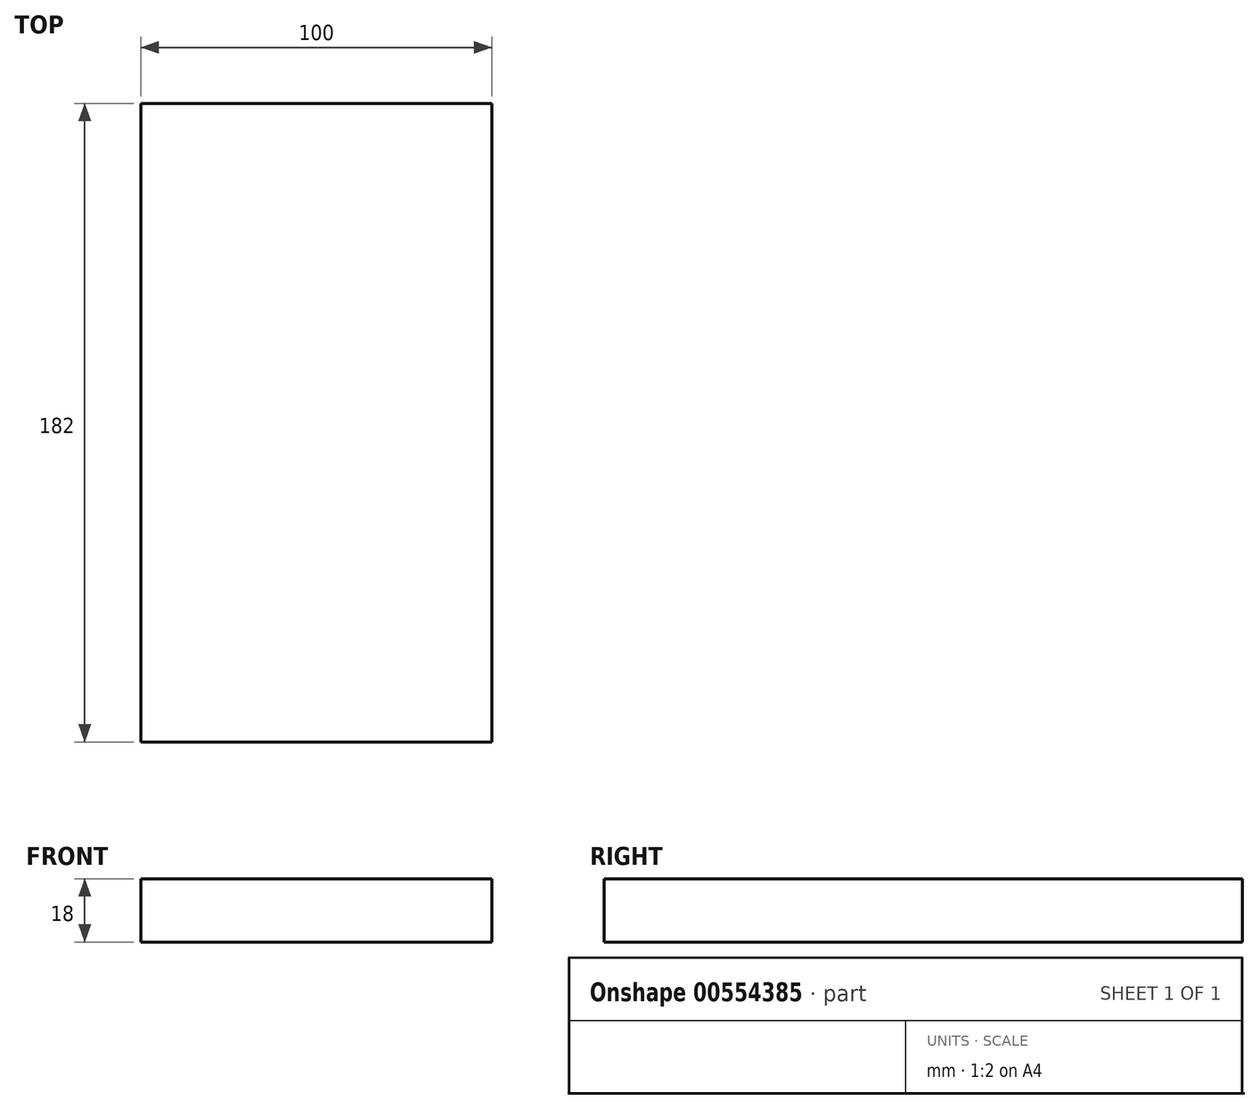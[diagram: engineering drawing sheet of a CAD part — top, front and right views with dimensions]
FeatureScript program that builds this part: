
annotation { "Feature Type Name" : "Feature", "Feature Type Description" : "" }
export const myFeature = defineFeature(function(context is Context, id is Id, definition is map)
    precondition{}
    {
        {
            var Q0;
            Q0=qCreatedBy(makeId("Top.planeOp"),FACE);
            var sketch = newSketch(context, id + "F0", { "sketchPlane" : qUnion([Q0])});
            skLineSegment(sketch, "E0.bottom", {"start": v(0, 0) * mm, "end": v(100, 0) * mm});
            skLineSegment(sketch, "E0.top", {"start": v(0, 182) * mm, "end": v(100, 182) * mm});
            skLineSegment(sketch, "E0.left", {"start": v(0, 0) * mm, "end": v(0, 182) * mm});
            skLineSegment(sketch, "E0.right", {"start": v(100, 0) * mm, "end": v(100, 182) * mm});
            skSolve(sketch);
        }
        {
            var Q0;
            Q0=makeQuery(id+"F0.imprint","IMPRINT",FACE,{"disambiguationData":[TD([[makeQuery(id+"F0.imprint","IMPRINT",EDGE,{"derivedFrom":sQuery(id+"F0.wireOp",EDGE,"E0.bottom")}),1.0]])]});
            extrude(context, id + "F1", {"entities" : qUnion([Q0]), "depth" : 18 * mm, "offsetDistance" : 25 * mm});
        }
    });
